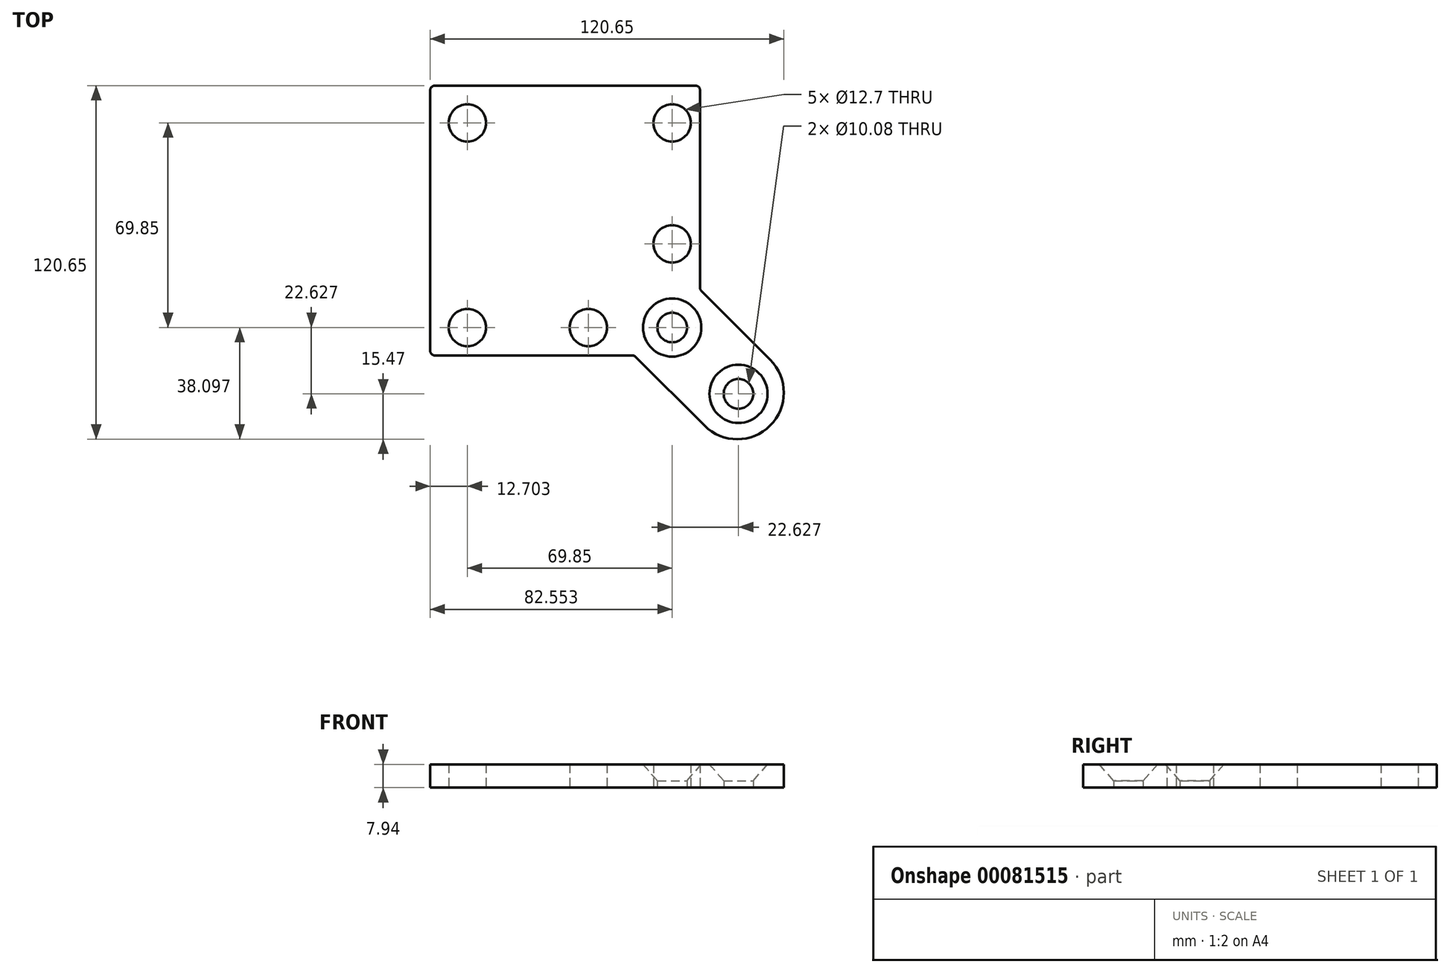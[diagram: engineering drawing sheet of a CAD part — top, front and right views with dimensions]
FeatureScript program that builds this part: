
annotation { "Feature Type Name" : "Feature", "Feature Type Description" : "" }
export const myFeature = defineFeature(function(context is Context, id is Id, definition is map)
    precondition{}
    {
        {
            var Q0;
            Q0=qCreatedBy(makeId("Top.planeOp"),FACE);
            var sketch = newSketch(context, id + "F0", { "sketchPlane" : qUnion([Q0])});
            skLineSegment(sketch, "E0.bottom", {"start": v(23.59, -46.04) * mm, "end": v(-46.04, -46.04) * mm});
            skLineSegment(sketch, "E0.top", {"start": v(46.04, 46.04) * mm, "end": v(-46.04, 46.04) * mm});
            skLineSegment(sketch, "E0.left", {"start": v(46.04, -23.59) * mm, "end": v(46.04, 46.04) * mm});
            skLineSegment(sketch, "E0.right", {"start": v(-46.04, -46.04) * mm, "end": v(-46.04, 46.04) * mm});
            skPoint(sketch, "E0.middle", {"position": v(0, 0) * mm});
            skArc(sketch, "E1", {"start": v(47.51, -69.96) * mm, "mid": v(69.96, -69.96) * mm, "end": v(69.96, -47.51) * mm});
            skLineSegment(sketch, "E2", {"start": v(47.51, -69.96) * mm, "end": v(23.59, -46.04) * mm});
            skLineSegment(sketch, "E3", {"start": v(69.96, -47.51) * mm, "end": v(46.04, -23.59) * mm});
            skSolve(sketch);
        }
        {
            var Q0;
            Q0=makeQuery(id+"F0.imprint","IMPRINT",FACE,{"disambiguationData":[TD([[makeQuery(id+"F0.imprint","IMPRINT",EDGE,{"derivedFrom":sQuery(id+"F0.wireOp",EDGE,"E0.bottom")}),-1.0]])]});
            extrude(context, id + "F1", {"entities" : qUnion([Q0]), "depth" : 7.94 * mm});
        }
        {
            var Q0;
            Q0=makeQuery(id+"F1.opExtrude","CAP_FACE",FACE,{"disambiguationData":[OSD([sQuery(id+"F0.wireOp",EDGE,"E0.bottom"),sQuery(id+"F0.wireOp",EDGE,"E0.top"),sQuery(id+"F0.wireOp",EDGE,"E0.left"),sQuery(id+"F0.wireOp",EDGE,"E0.right"),sQuery(id+"F0.wireOp",EDGE,"E1"),sQuery(id+"F0.wireOp",EDGE,"E2"),sQuery(id+"F0.wireOp",EDGE,"E3")])],"isStart":false});
            var sketch = newSketch(context, id + "F2", { "sketchPlane" : qUnion([Q0])});
            skPoint(sketch, "E4", {"position": v(-33.34, 33.34) * mm});
            skPoint(sketch, "E5", {"position": v(36.51, 33.34) * mm});
            skPoint(sketch, "E6", {"position": v(36.51, -7.94) * mm});
            skPoint(sketch, "E7", {"position": v(7.94, -36.51) * mm});
            skPoint(sketch, "E8", {"position": v(-33.34, -36.51) * mm});
            skSolve(sketch);
        }
        {
            var Q0;
            Q0=sQuery(id+"F2.wireOp",VERTEX,"E4");
            var Q1;
            Q1=sQuery(id+"F2.wireOp",VERTEX,"E8");
            var Q2;
            Q2=sQuery(id+"F2.wireOp",VERTEX,"E7");
            var Q3;
            Q3=sQuery(id+"F2.wireOp",VERTEX,"E6");
            var Q4;
            Q4=sQuery(id+"F2.wireOp",VERTEX,"E5");
            var Q5;
            Q5=makeQuery(id+"F1.opExtrude","SWEPT_BODY",BODY,{"disambiguationData":[OSD([sQuery(id+"F0.wireOp",EDGE,"E0.bottom"),sQuery(id+"F0.wireOp",EDGE,"E0.top"),sQuery(id+"F0.wireOp",EDGE,"E0.left"),sQuery(id+"F0.wireOp",EDGE,"E0.right"),sQuery(id+"F0.wireOp",EDGE,"E1"),sQuery(id+"F0.wireOp",EDGE,"E2"),sQuery(id+"F0.wireOp",EDGE,"E3")])]});
            hole(context, id + "F3", {"style" : HoleStyle.SIMPLE, "endStyle" : HoleEndStyle.THROUGH, "holeDiameter" : 12.7 * mm, "locations" : qUnion([Q0, Q1, Q2, Q3, Q4]), "scope" : qUnion([Q5]), "isTappedThrough" : true, "startStyle" : HoleStartStyle.PART});
        }
        {
            var Q0;
            Q0=makeQuery(id+"F1.opExtrude","CAP_FACE",FACE,{"disambiguationData":[OSD([sQuery(id+"F0.wireOp",EDGE,"E0.bottom"),sQuery(id+"F0.wireOp",EDGE,"E0.top"),sQuery(id+"F0.wireOp",EDGE,"E0.left"),sQuery(id+"F0.wireOp",EDGE,"E0.right"),sQuery(id+"F0.wireOp",EDGE,"E1"),sQuery(id+"F0.wireOp",EDGE,"E2"),sQuery(id+"F0.wireOp",EDGE,"E3")])],"isStart":false});
            var sketch = newSketch(context, id + "F4", { "sketchPlane" : qUnion([Q0])});
            skPoint(sketch, "E9", {"position": v(36.51, -36.51) * mm});
            skPoint(sketch, "E10", {"position": v(59.14, -59.14) * mm});
            skLineSegment(sketch, "E11", {"start": v(36.51, -36.51) * mm, "end": v(36.51, -75.26) * mm, "construction": true});
            skLineSegment(sketch, "E12", {"start": v(59.14, -59.14) * mm, "end": v(36.51, -59.14) * mm, "construction": true});
            skLineSegment(sketch, "E13", {"start": v(36.51, -36.51) * mm, "end": v(59.14, -59.14) * mm, "construction": true});
            skSolve(sketch);
        }
        {
            var Q0;
            Q0=sQuery(id+"F4.wireOp",VERTEX,"E9");
            var Q1;
            Q1=sQuery(id+"F4.wireOp",VERTEX,"E10");
            var Q2;
            Q2=makeQuery(id+"F1.opExtrude","SWEPT_BODY",BODY,{"disambiguationData":[OSD([sQuery(id+"F0.wireOp",EDGE,"E0.bottom"),sQuery(id+"F0.wireOp",EDGE,"E0.top"),sQuery(id+"F0.wireOp",EDGE,"E0.left"),sQuery(id+"F0.wireOp",EDGE,"E0.right"),sQuery(id+"F0.wireOp",EDGE,"E1"),sQuery(id+"F0.wireOp",EDGE,"E2"),sQuery(id+"F0.wireOp",EDGE,"E3")])]});
            hole(context, id + "F5", {"style" : HoleStyle.C_SINK, "endStyle" : HoleEndStyle.THROUGH, "standardTappedOrClearance" : lookupTablePath({ "standard" : "ANSI", "fit" : "Normal (ASME)", "size" : "3/8", "type" : "Clearance" }), "standardBlindInLast" : lookupTablePath({ "fit" : "Free", "standard" : "ANSI", "size" : "3/8", "type" : "Clearance" }), "holeDiameter" : 10.08 * mm, "cSinkDiameter" : 19.84 * mm, "cSinkAngle" : 82 * degree, "locations" : qUnion([Q0, Q1]), "scope" : qUnion([Q2]), "isTappedThrough" : true, "startStyle" : HoleStartStyle.SKETCH});
        }
        {
            var Q0;
            Q0=makeQuery(id+"F1.opExtrude","SWEPT_EDGE",EDGE,{"disambiguationData":[OSD([sQuery(id+"F0.wireOp",EDGE,"E0.bottom"),sQuery(id+"F0.wireOp",EDGE,"E0.right")])]});
            var Q1;
            Q1=makeQuery(id+"F1.opExtrude","SWEPT_EDGE",EDGE,{"disambiguationData":[OSD([sQuery(id+"F0.wireOp",EDGE,"E0.top"),sQuery(id+"F0.wireOp",EDGE,"E0.right")])]});
            var Q2;
            Q2=makeQuery(id+"F1.opExtrude","SWEPT_EDGE",EDGE,{"disambiguationData":[OSD([sQuery(id+"F0.wireOp",EDGE,"E0.top"),sQuery(id+"F0.wireOp",EDGE,"E0.left")])]});
            var Q3;
            Q3=makeQuery(id+"F1.opExtrude","SWEPT_EDGE",EDGE,{"disambiguationData":[OSD([sQuery(id+"F0.wireOp",EDGE,"E0.left"),sQuery(id+"F0.wireOp",EDGE,"E3")])]});
            var Q4;
            Q4=makeQuery(id+"F1.opExtrude","SWEPT_EDGE",EDGE,{"disambiguationData":[OSD([sQuery(id+"F0.wireOp",EDGE,"E0.bottom"),sQuery(id+"F0.wireOp",EDGE,"E2")])]});
            fillet(context, id + "F6", {"entities" : qUnion([Q0, Q1, Q2, Q3, Q4]), "radius" : 1.59 * mm, "tangentPropagation" : true, "allowEdgeOverflow" : false});
        }
    });
